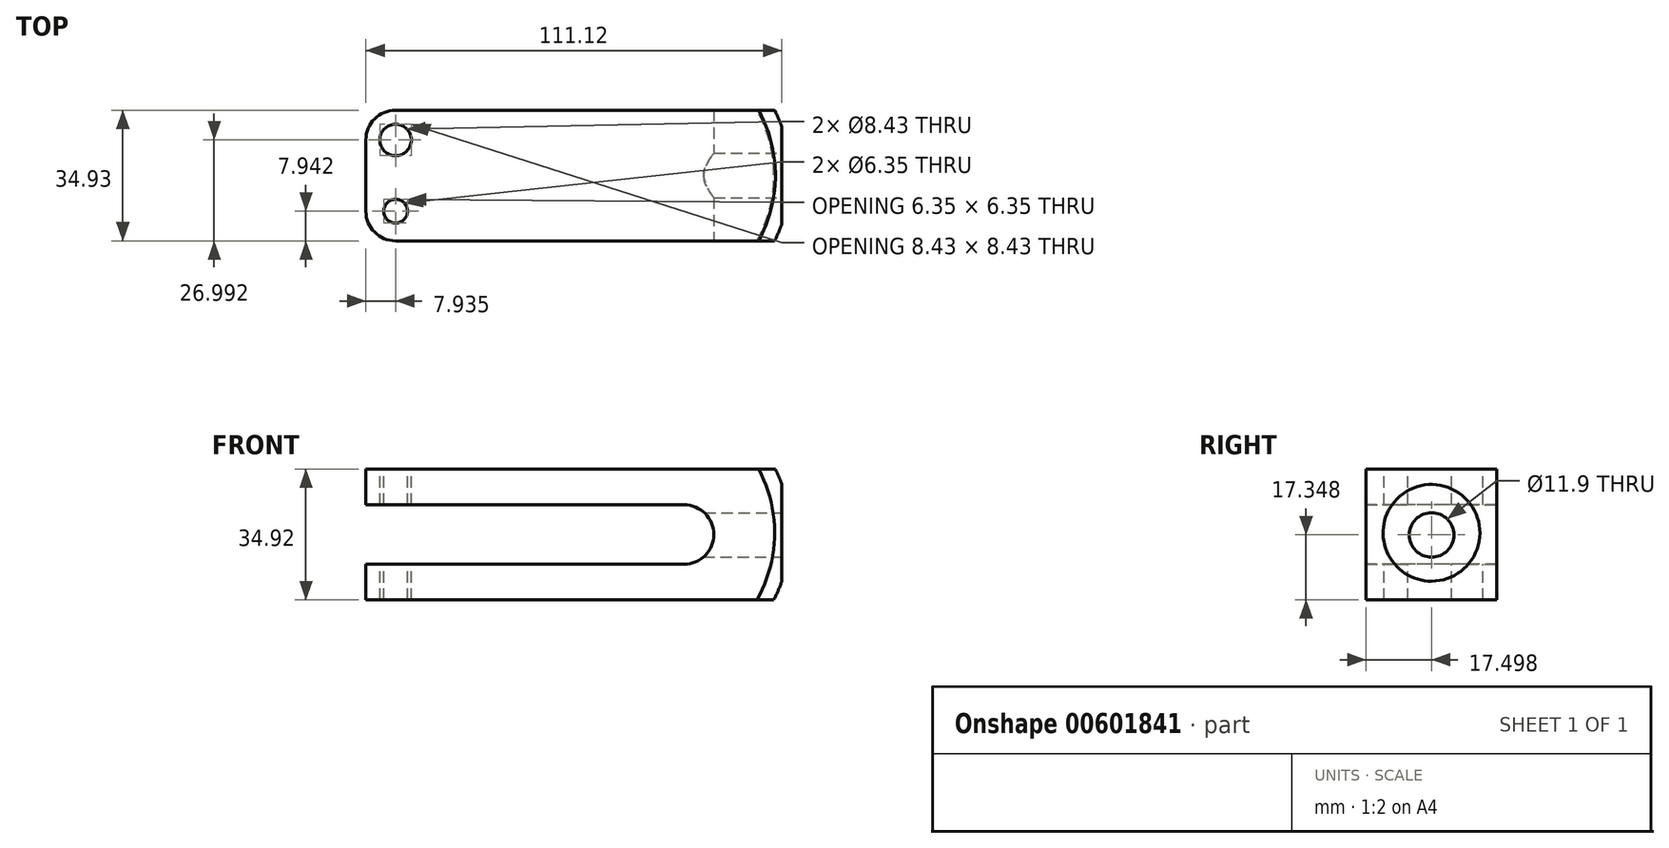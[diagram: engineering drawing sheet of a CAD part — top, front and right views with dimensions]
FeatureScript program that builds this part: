
annotation { "Feature Type Name" : "Feature", "Feature Type Description" : "" }
export const myFeature = defineFeature(function(context is Context, id is Id, definition is map)
    precondition{}
    {
        {
            var Q0;
            Q0=qCreatedBy(makeId("Front.planeOp"),FACE);
            var sketch = newSketch(context, id + "F0", { "sketchPlane" : qUnion([Q0])});
            skLineSegment(sketch, "E0.bottom", {"start": v(-57.55, 7.14) * mm, "end": v(53.57, 7.14) * mm});
            skLineSegment(sketch, "E0.top", {"start": v(-57.55, -27.78) * mm, "end": v(53.57, -27.78) * mm});
            skLineSegment(sketch, "E0.left", {"start": v(-57.55, 7.14) * mm, "end": v(-57.55, -27.78) * mm});
            skLineSegment(sketch, "E0.right", {"start": v(53.57, 7.14) * mm, "end": v(53.57, -27.78) * mm});
            skSolve(sketch);
        }
        {
            var Q0;
            Q0=makeQuery(id+"F0.imprint","IMPRINT",FACE,{"disambiguationData":[TD([[makeQuery(id+"F0.imprint","IMPRINT",EDGE,{"derivedFrom":sQuery(id+"F0.wireOp",EDGE,"E0.bottom")}),-1.0]])]});
            extrude(context, id + "F1", {"entities" : qUnion([Q0]), "depth" : 34.92 * mm, "offsetDistance" : 25.4 * mm});
        }
        {
            var Q0;
            Q0=makeQuery(id+"F1.opExtrude","CAP_FACE",FACE,{"disambiguationData":[OSD([sQuery(id+"F0.wireOp",EDGE,"E0.bottom"),sQuery(id+"F0.wireOp",EDGE,"E0.top"),sQuery(id+"F0.wireOp",EDGE,"E0.left"),sQuery(id+"F0.wireOp",EDGE,"E0.right")])],"isStart":false});
            var sketch = newSketch(context, id + "F2", { "sketchPlane" : qUnion([Q0])});
            skLineSegment(sketch, "E1.bottom", {"start": v(-57.55, -2.38) * mm, "end": v(27.46, -2.38) * mm});
            skLineSegment(sketch, "E1.top", {"start": v(-57.55, -18.26) * mm, "end": v(27.46, -18.26) * mm});
            skArc(sketch, "E2", {"start": v(27.46, -18.26) * mm, "mid": v(35.4, -10.32) * mm, "end": v(27.46, -2.38) * mm});
            skLineSegment(sketch, "E3", {"start": v(-57.55, -2.38) * mm, "end": v(-57.55, -18.26) * mm});
            skSolve(sketch);
        }
        {
            var Q0;
            Q0 = qSketchRegion(id + "F2", true);
            extrude(context, id + "F3", {"entities" : qUnion([Q0]), "operationType" : NewBodyOperationType.REMOVE, "oppositeDirection" : true, "depth" : 34.92 * mm, "offsetDistance" : 25.4 * mm});
        }
        {
            var Q0;
            Q0=makeQuery(id+"F1.opExtrude","CAP_FACE",FACE,{"disambiguationData":[OSD([sQuery(id+"F0.wireOp",EDGE,"E0.bottom"),sQuery(id+"F0.wireOp",EDGE,"E0.top"),sQuery(id+"F0.wireOp",EDGE,"E0.left"),sQuery(id+"F0.wireOp",EDGE,"E0.right")])],"isStart":false});
            var Q1;
            Q1=makeQuery(id+"F1.opExtrude","CAP_FACE",FACE,{"disambiguationData":[OSD([sQuery(id+"F0.wireOp",EDGE,"E0.bottom"),sQuery(id+"F0.wireOp",EDGE,"E0.top"),sQuery(id+"F0.wireOp",EDGE,"E0.left"),sQuery(id+"F0.wireOp",EDGE,"E0.right")])],"isStart":true});
            cPlane(context, id + "F4", {"entities" : qUnion([Q0, Q1]), "cplaneType" : CPlaneType.MID_PLANE, "offset" : 25.4 * mm, "width" : 152.4 * mm, "height" : 152.4 * mm});
        }
        {
            var Q0;
            Q0=qCreatedBy(id+"F4.planeOp",FACE);
            var sketch = newSketch(context, id + "F5", { "sketchPlane" : qUnion([Q0])});
            skLineSegment(sketch, "E4", {"start": v(56.13, -9.87) * mm, "end": v(-68.8, -9.87) * mm});
            skLineSegment(sketch, "E5", {"start": v(-68.8, -9.87) * mm, "end": v(-68.8, 17.7) * mm});
            skLineSegment(sketch, "E6", {"start": v(-68.8, 17.7) * mm, "end": v(44.74, 17.7) * mm});
            skArc(sketch, "E7", {"start": v(56.13, -9.87) * mm, "mid": v(52.85, 4.91) * mm, "end": v(44.74, 17.7) * mm});
            skSolve(sketch);
        }
        {
            var Q0;
            Q0=makeQuery(id+"F5.imprint","IMPRINT",FACE,{"disambiguationData":[TD([[makeQuery(id+"F5.imprint","IMPRINT",EDGE,{"derivedFrom":sQuery(id+"F5.wireOp",EDGE,"E4")}),-1.0]])]});
            var Q1;
            Q1=sQuery(id+"F5.wireOp",EDGE,"E4");
            revolve(context, id + "F6", {"operationType" : NewBodyOperationType.INTERSECT, "entities" : qUnion([Q0]), "axis" : qUnion([Q1]), "revolveType" : RevolveType.FULL});
        }
        {
            var Q0;
            Q0=makeQuery(id+"F1.opExtrude","SWEPT_FACE",FACE,{"disambiguationData":[OSD([sQuery(id+"F0.wireOp",EDGE,"E0.bottom")])]});
            var sketch = newSketch(context, id + "F7", { "sketchPlane" : qUnion([Q0])});
            skPoint(sketch, "E8", {"position": v(-49.61, -7.94) * mm});
            skPoint(sketch, "E9", {"position": v(-49.61, -26.99) * mm});
            skSolve(sketch);
        }
        {
            var Q0;
            Q0=sQuery(id+"F7.wireOp",VERTEX,"E8");
            var Q1;
            Q1=makeQuery(id+"F1.opExtrude","SWEPT_BODY",BODY,{"disambiguationData":[OSD([sQuery(id+"F0.wireOp",EDGE,"E0.bottom"),sQuery(id+"F0.wireOp",EDGE,"E0.top"),sQuery(id+"F0.wireOp",EDGE,"E0.left"),sQuery(id+"F0.wireOp",EDGE,"E0.right")])]});
            hole(context, id + "F8", {"style" : HoleStyle.SIMPLE, "endStyle" : HoleEndStyle.THROUGH, "standardTappedOrClearance" : lookupTablePath({ "standard" : "ANSI", "fit" : "Normal (ASME)", "size" : "5/16", "type" : "Clearance" }), "standardBlindInLast" : lookupTablePath({ "fit" : "Free", "standard" : "ANSI", "size" : "5/16", "type" : "Clearance" }), "holeDiameter" : 8.43 * mm, "majorDiameter" : 6.35 * mm, "isTappedThrough" : true, "tappedDepth" : 12.7 * mm, "tapClearance" : 3, "locations" : qUnion([Q0]), "scope" : qUnion([Q1])});
        }
        {
            var Q0;
            Q0=sQuery(id+"F7.wireOp",VERTEX,"E9");
            var Q1;
            Q1=makeQuery(id+"F1.opExtrude","SWEPT_BODY",BODY,{"disambiguationData":[OSD([sQuery(id+"F0.wireOp",EDGE,"E0.bottom"),sQuery(id+"F0.wireOp",EDGE,"E0.top"),sQuery(id+"F0.wireOp",EDGE,"E0.left"),sQuery(id+"F0.wireOp",EDGE,"E0.right")])]});
            hole(context, id + "F9", {"style" : HoleStyle.SIMPLE, "endStyle" : HoleEndStyle.THROUGH, "holeDiameter" : 6.35 * mm, "majorDiameter" : 6.35 * mm, "isTappedThrough" : true, "tappedDepth" : 12.7 * mm, "tapClearance" : 3, "locations" : qUnion([Q0]), "scope" : qUnion([Q1])});
        }
        {
            var Q0;
            {var subQ0=sQuery(id+"F0.wireOp",EDGE,"E0.bottom");var subQ1=sQuery(id+"F0.wireOp",EDGE,"E0.left");Q0=makeQuery(id+"F3.boolean.opBoolean","SPLIT",EDGE,{"disambiguationData":[TD([makeQuery(id+"F1.opExtrude","SWEPT_FACE",FACE,{"disambiguationData":[OSD([subQ0])]})])],"derivedFrom":makeQuery(id+"F1.opExtrude","CAP_EDGE",EDGE,{"disambiguationData":[OSD([subQ1])],"isStart":true})});}
            var Q1;
            {var subQ0=sQuery(id+"F0.wireOp",EDGE,"E0.bottom");var subQ1=sQuery(id+"F0.wireOp",EDGE,"E0.left");Q1=makeQuery(id+"F3.boolean.opBoolean","SPLIT",EDGE,{"disambiguationData":[TD([makeQuery(id+"F1.opExtrude","SWEPT_FACE",FACE,{"disambiguationData":[OSD([subQ0])]})])],"derivedFrom":makeQuery(id+"F1.opExtrude","CAP_EDGE",EDGE,{"disambiguationData":[OSD([subQ1])],"isStart":false})});}
            var Q2;
            {var subQ0=sQuery(id+"F0.wireOp",EDGE,"E0.left");var subQ1=sQuery(id+"F0.wireOp",EDGE,"E0.top");Q2=makeQuery(id+"F3.boolean.opBoolean","SPLIT",EDGE,{"disambiguationData":[TD([makeQuery(id+"F1.opExtrude","SWEPT_FACE",FACE,{"disambiguationData":[OSD([subQ1])]})])],"derivedFrom":makeQuery(id+"F1.opExtrude","CAP_EDGE",EDGE,{"disambiguationData":[OSD([subQ0])],"isStart":true})});}
            var Q3;
            {var subQ0=sQuery(id+"F0.wireOp",EDGE,"E0.left");var subQ1=sQuery(id+"F0.wireOp",EDGE,"E0.top");Q3=makeQuery(id+"F3.boolean.opBoolean","SPLIT",EDGE,{"disambiguationData":[TD([makeQuery(id+"F1.opExtrude","SWEPT_FACE",FACE,{"disambiguationData":[OSD([subQ1])]})])],"derivedFrom":makeQuery(id+"F1.opExtrude","CAP_EDGE",EDGE,{"disambiguationData":[OSD([subQ0])],"isStart":false})});}
            fillet(context, id + "F10", {"entities" : qUnion([Q0, Q1, Q2, Q3]), "radius" : 7.94 * mm, "tangentPropagation" : true, "allowEdgeOverflow" : false});
        }
        {
            var Q0;
            Q0=makeQuery(id+"F1.opExtrude","SWEPT_FACE",FACE,{"disambiguationData":[OSD([sQuery(id+"F0.wireOp",EDGE,"E0.right")])]});
            var sketch = newSketch(context, id + "F11", { "sketchPlane" : qUnion([Q0])});
            skLineSegment(sketch, "E10.bottom", {"start": v(-34.86, 7.17) * mm, "end": v(0, 7.17) * mm});
            skLineSegment(sketch, "E10.top", {"start": v(-34.86, -28.03) * mm, "end": v(0, -28.03) * mm});
            skLineSegment(sketch, "E10.left", {"start": v(-34.86, 7.17) * mm, "end": v(-34.86, -28.03) * mm});
            skLineSegment(sketch, "E10.right", {"start": v(0, 7.17) * mm, "end": v(0, -28.03) * mm});
            skLineSegment(sketch, "E11", {"start": v(-34.86, 7.17) * mm, "end": v(0, -28.03) * mm, "construction": true});
            skLineSegment(sketch, "E12", {"start": v(-34.86, -28.03) * mm, "end": v(0, 7.17) * mm, "construction": true});
            skLineSegment(sketch, "E13", {"start": v(-17.43, 7.17) * mm, "end": v(-17.43, -28.03) * mm, "construction": true});
            skLineSegment(sketch, "E14", {"start": v(-34.86, -10.43) * mm, "end": v(0, -10.43) * mm, "construction": true});
            skPoint(sketch, "E15", {"position": v(-17.43, -10.43) * mm});
            skSolve(sketch);
        }
        {
            var Q0;
            Q0=sQuery(id+"F11.wireOp",VERTEX,"E15");
            var Q1;
            Q1=makeQuery(id+"F1.opExtrude","SWEPT_BODY",BODY,{"disambiguationData":[OSD([sQuery(id+"F0.wireOp",EDGE,"E0.bottom"),sQuery(id+"F0.wireOp",EDGE,"E0.top"),sQuery(id+"F0.wireOp",EDGE,"E0.left"),sQuery(id+"F0.wireOp",EDGE,"E0.right")])]});
            hole(context, id + "F12", {"style" : HoleStyle.SIMPLE, "endStyle" : HoleEndStyle.THROUGH, "standardTappedOrClearance" : lookupTablePath({ "standard" : "ANSI", "fit" : "Normal (ASME)", "size" : "7/16", "type" : "Clearance" }), "standardBlindInLast" : lookupTablePath({ "fit" : "Free", "standard" : "ANSI", "size" : "7/16", "type" : "Clearance" }), "holeDiameter" : 11.9 * mm, "majorDiameter" : 6.35 * mm, "isTappedThrough" : true, "tappedDepth" : 12.7 * mm, "tapClearance" : 3, "locations" : qUnion([Q0]), "scope" : qUnion([Q1])});
        }
    });
